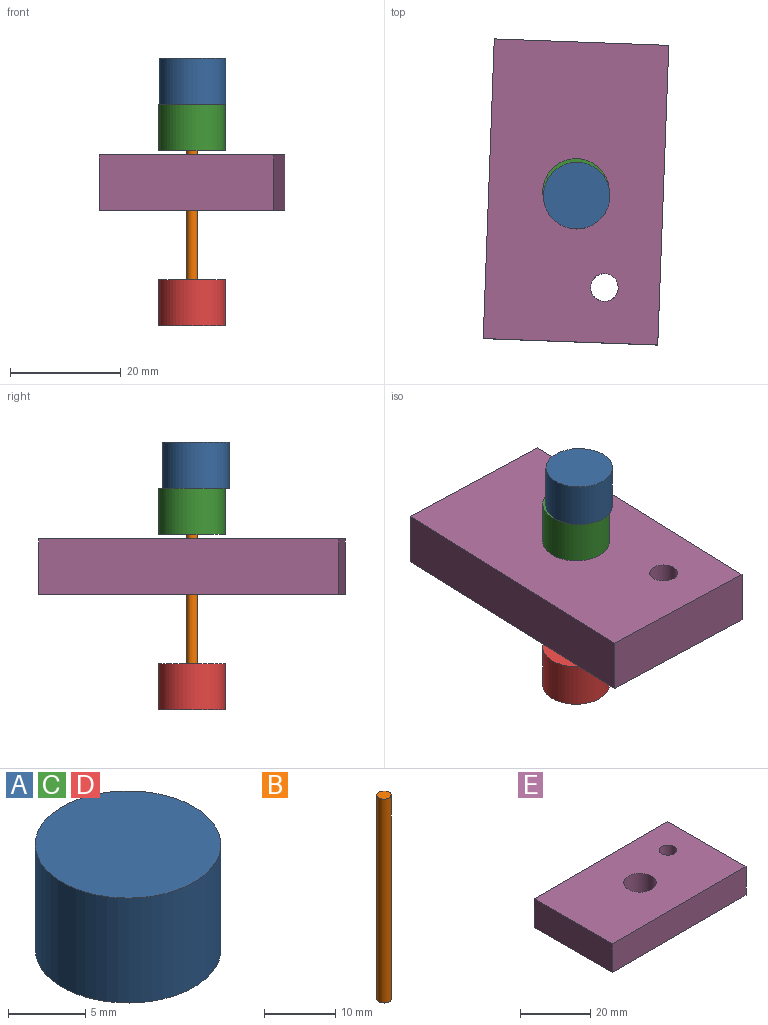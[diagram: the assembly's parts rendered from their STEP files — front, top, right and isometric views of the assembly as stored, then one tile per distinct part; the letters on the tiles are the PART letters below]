
ASSEMBLY  parts=5 mates=3
PART A: 3 faces, bbox 12x12x8.3 mm
  f0: cylinder r=6mm len=12mm, axis (0,0,-1), area 312.9mm2, adj f1,f2
  f1: plane 12x12mm, normal (0,0,1), area 113.1mm2, adj f0
  f2: plane 12x12mm, normal (0,0,-1), area 113.1mm2, adj f0
PART B: 3 faces, bbox 2x2x35 mm
  f0: plane 2x2mm, normal (0,0,-1), area 3.1mm2, adj f1
  f1: cylinder r=1mm len=35mm, axis (0,0,1), area 219.9mm2, adj f0,f2
  f2: plane 2x2mm, normal (0,0,1), area 3.1mm2, adj f1
PART C: same geometry as A
PART D: same geometry as A
PART E: 9 faces, bbox 54.1x31.5x10 mm
  f0: plane 54.06x31.48mm, normal (0,0,1), area 1614.5mm2, adj f2,f3,f4,f5,f6,f7
  f1: plane 54.06x31.48mm, normal (0,0,-1), area 1555.6mm2, adj f2,f3,f4,f5,f6,f8
  f2: plane 54.06x10mm, normal (0,-1,0), area 540.6mm2, adj f0,f1,f3,f5
  f3: plane 31.48x10mm, normal (1,0,0), area 314.8mm2, adj f0,f1,f2,f4
  f4: plane 54.06x10mm, normal (0,1,0), area 540.6mm2, adj f0,f1,f3,f5
  f5: plane 31.48x10mm, normal (-1,0,0), area 314.8mm2, adj f0,f1,f2,f4
  f6: cylinder r=4.65mm len=10mm, axis (0,0,-1), area 292mm2, adj f0,f1
  f7: cylinder r=2.5mm len=7.5mm, axis (0,0,-1), area 117.8mm2, adj f0,f8
  f8: cone r=2.5mm half-angle=45deg, axis (0,0,-1), area 83.3mm2, adj f1,f7
PLACE A rot(axis=(0,0,-1),125.5deg) t=(0.12,-0.7,-11.25)mm
PLACE B rot(axis=(0,0,-1),61.8deg) t=(0,0,-12.5)mm fixed
PLACE C rot(axis=(0,0,-1),125.5deg) t=(0,0,-19.55)mm
PLACE D rot(axis=(0,0,-1),61.8deg) t=(0,0,-51.2)mm
PLACE E rot(axis=(0,0,-1),92.1deg) t=(0,0,0)mm
MATE planar A.f0 <-> C.f0  axis (0,0,-1) through (0.12,-0.7,19.15)mm
MATE cylindrical B.f1 <-> C.f0  axis (0,0,1) through (0,0,5)mm
MATE revolute B.f1 <-> E.f6  axis (0,0,1) through (0,0,5)mm
